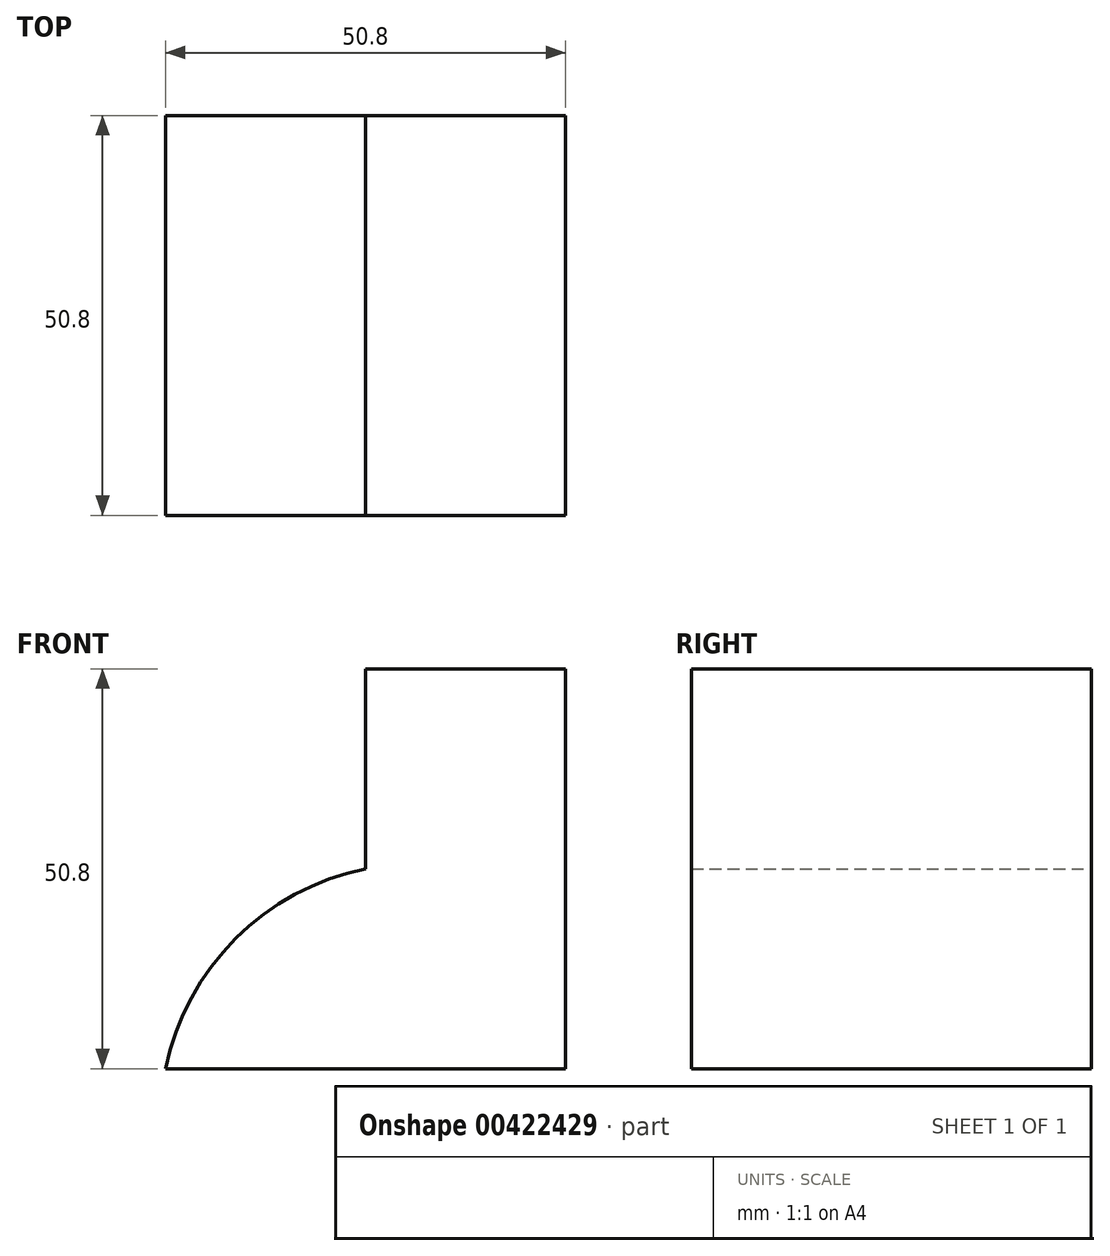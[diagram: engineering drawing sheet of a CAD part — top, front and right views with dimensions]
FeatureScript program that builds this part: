
annotation { "Feature Type Name" : "Feature", "Feature Type Description" : "" }
export const myFeature = defineFeature(function(context is Context, id is Id, definition is map)
    precondition{}
    {
        {
            var Q0;
            Q0=qCreatedBy(makeId("Front.planeOp"),FACE);
            var sketch = newSketch(context, id + "F0", { "sketchPlane" : qUnion([Q0])});
            skLineSegment(sketch, "E0", {"start": v(0, 0) * mm, "end": v(0, 50.8) * mm});
            skLineSegment(sketch, "E1", {"start": v(0, 0) * mm, "end": v(-50.8, 0) * mm});
            skLineSegment(sketch, "E2", {"start": v(0, 50.8) * mm, "end": v(-25.4, 50.8) * mm});
            skLineSegment(sketch, "E3", {"start": v(-25.4, 50.8) * mm, "end": v(-25.4, 25.4) * mm});
            skArc(sketch, "E4", {"start": v(-25.4, 25.4) * mm, "mid": v(-41.92, 16.52) * mm, "end": v(-50.8, 0) * mm});
            skSolve(sketch);
        }
        {
            var Q0;
            Q0=makeQuery(id+"F0.imprint","IMPRINT",FACE,{"disambiguationData":[TD([[makeQuery(id+"F0.imprint","IMPRINT",EDGE,{"derivedFrom":sQuery(id+"F0.wireOp",EDGE,"E0")}),1.0]])]});
            extrude(context, id + "F1", {"entities" : qUnion([Q0]), "depth" : 50.8 * mm});
        }
    });
